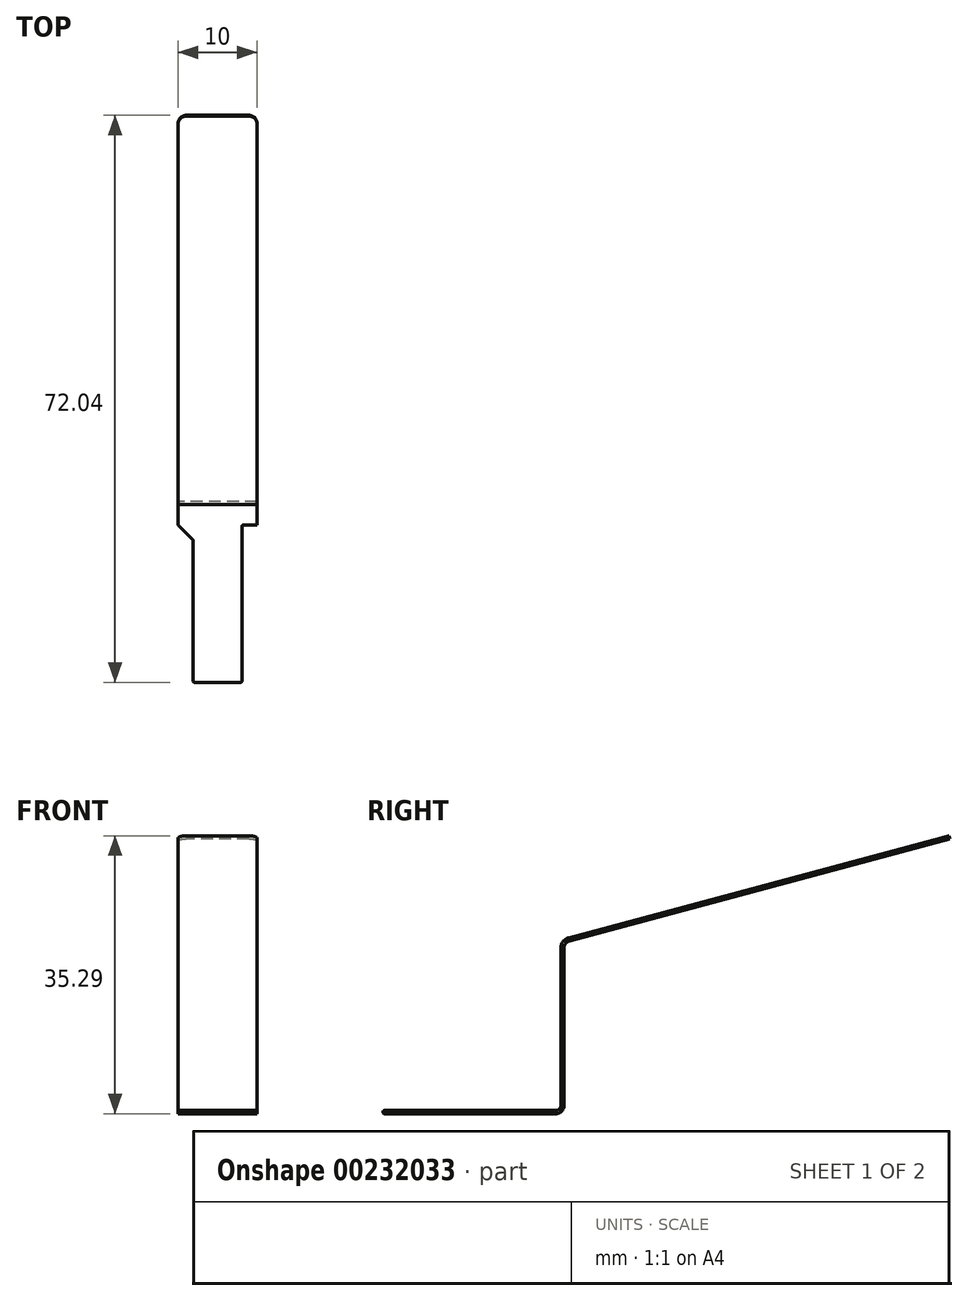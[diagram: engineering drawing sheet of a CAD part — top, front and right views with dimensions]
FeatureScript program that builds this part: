
annotation { "Feature Type Name" : "Feature", "Feature Type Description" : "" }
export const myFeature = defineFeature(function(context is Context, id is Id, definition is map)
    precondition{}
    {
        {
            var Q0;
            Q0=qCreatedBy(makeId("Front.planeOp"),FACE);
            var sketch = newSketch(context, id + "F0", { "sketchPlane" : qUnion([Q0])});
            skLineSegment(sketch, "E0.bottom", {"start": v(-3.12, 0) * mm, "end": v(3.12, 0) * mm});
            skLineSegment(sketch, "E0.top", {"start": v(-3.12, 0.4) * mm, "end": v(3.12, 0.4) * mm});
            skLineSegment(sketch, "E0.left", {"start": v(-3.12, 0) * mm, "end": v(-3.12, 0.4) * mm});
            skLineSegment(sketch, "E0.right", {"start": v(3.12, 0) * mm, "end": v(3.12, 0.4) * mm});
            skSolve(sketch);
        }
        {
            var Q0;
            Q0=qCreatedBy(makeId("Right.planeOp"),FACE);
            var sketch = newSketch(context, id + "F1", { "sketchPlane" : qUnion([Q0])});
            skLineSegment(sketch, "E1", {"start": v(0, 0) * mm, "end": v(20, 0) * mm});
            skSolve(sketch);
        }
        {
            var Q0;
            Q0=makeQuery(id+"F0.imprint","IMPRINT",FACE,{"disambiguationData":[TD([[makeQuery(id+"F0.imprint","IMPRINT",EDGE,{"derivedFrom":sQuery(id+"F0.wireOp",EDGE,"E0.bottom")}),1.0]])]});
            var Q1;
            Q1=sQuery(id+"F1.wireOp",EDGE,"E1");
            sweep(context, id + "F2", {"profiles" : qUnion([Q0]), "path" : qUnion([Q1])});
        }
        {
            var Q0;
            Q0=makeQuery(id+"F2.opSweep","CAP_FACE",FACE,{"disambiguationData":[OSD([sQuery(id+"F0.wireOp",EDGE,"E0.bottom"),sQuery(id+"F0.wireOp",EDGE,"E0.top"),sQuery(id+"F0.wireOp",EDGE,"E0.left"),sQuery(id+"F0.wireOp",EDGE,"E0.right"),sQuery(id+"F1.wireOp",VERTEX,"E1.end")])],"isStart":false});
            var sketch = newSketch(context, id + "F3", { "sketchPlane" : qUnion([Q0])});
            skLineSegment(sketch, "E2.bottom", {"start": v(-5, 0) * mm, "end": v(5, 0) * mm});
            skLineSegment(sketch, "E2.top", {"start": v(-5, 0.4) * mm, "end": v(5, 0.4) * mm});
            skLineSegment(sketch, "E2.left", {"start": v(-5, 0) * mm, "end": v(-5, 0.4) * mm});
            skLineSegment(sketch, "E2.right", {"start": v(5, 0) * mm, "end": v(5, 0.4) * mm});
            skSolve(sketch);
        }
        {
            var Q0;
            Q0=qCreatedBy(makeId("Right.planeOp"),FACE);
            var sketch = newSketch(context, id + "F4", { "sketchPlane" : qUnion([Q0])});
            skLineSegment(sketch, "E3", {"start": v(20, 0) * mm, "end": v(22, 0) * mm});
            skArc(sketch, "E4", {"start": v(22, 0) * mm, "mid": v(22.7, 0.3) * mm, "end": v(23, 1) * mm});
            skLineSegment(sketch, "E5", {"start": v(23, 1) * mm, "end": v(23, 21) * mm});
            skArc(sketch, "E6", {"start": v(23, 21) * mm, "mid": v(23.2, 21.6) * mm, "end": v(23.74, 21.97) * mm});
            skLineSegment(sketch, "E7", {"start": v(23.74, 21.97) * mm, "end": v(72.04, 34.9) * mm});
            skSolve(sketch);
        }
        {
            var Q0;
            {var subQ2=sQuery(id+"F3.wireOp",EDGE,"E2.left");Q0=makeQuery(id+"F3.imprint","IMPRINT",FACE,{"disambiguationData":[TD([[makeQuery(id+"F3.imprint","IMPRINT",EDGE,{"derivedFrom":subQ2}),-1.0]])]});}
            var Q1;
            {var subQ1=sQuery(id+"F1.wireOp",VERTEX,"E1.end");var subQ2=makeQuery(id+"F2.opSweep","CAP_EDGE",EDGE,{"disambiguationData":[OSD([sQuery(id+"F0.wireOp",EDGE,"E0.left"),subQ1])],"isStart":false});Q1=makeQuery(id+"F3.imprint","IMPRINT",FACE,{"disambiguationData":[TD([[makeQuery(id+"F3.imprint","IMPRINT",EDGE,{"derivedFrom":subQ2}),1.0]])]});}
            var Q2;
            {var subQ2=sQuery(id+"F3.wireOp",EDGE,"E2.right");Q2=makeQuery(id+"F3.imprint","IMPRINT",FACE,{"disambiguationData":[TD([[makeQuery(id+"F3.imprint","IMPRINT",EDGE,{"derivedFrom":subQ2}),1.0]])]});}
            var Q3;
            Q3=sQuery(id+"F4.wireOp",EDGE,"E3");
            var Q4;
            Q4=sQuery(id+"F4.wireOp",EDGE,"E4");
            var Q5;
            Q5=sQuery(id+"F4.wireOp",EDGE,"E5");
            var Q6;
            Q6=sQuery(id+"F4.wireOp",EDGE,"E7");
            var Q7;
            Q7=sQuery(id+"F4.wireOp",EDGE,"E6");
            sweep(context, id + "F5", {"operationType" : NewBodyOperationType.ADD, "profiles" : qUnion([Q0, Q1, Q2]), "path" : qUnion([Q3, Q4, Q5, Q6, Q7])});
        }
        {
            var Q0;
            Q0=makeQuery(id+"F2.opSweep","CAP_EDGE",EDGE,{"disambiguationData":[OSD([sQuery(id+"F0.wireOp",EDGE,"E0.right"),sQuery(id+"F1.wireOp",VERTEX,"E1.end")])],"isStart":false});
            var Q1;
            Q1=makeQuery(id+"F2.opSweep","CAP_EDGE",EDGE,{"disambiguationData":[OSD([sQuery(id+"F0.wireOp",EDGE,"E0.left"),sQuery(id+"F1.wireOp",VERTEX,"E1.end")])],"isStart":false});
            chamfer(context, id + "F6", {"entities" : qUnion([Q0, Q1]), "width" : 1.89 * mm, "tangentPropagation" : true});
        }
        {
            var Q0;
            Q0=makeQuery(id+"F2.opSweep","CAP_EDGE",EDGE,{"disambiguationData":[OSD([sQuery(id+"F0.wireOp",EDGE,"E0.right"),sQuery(id+"F1.wireOp",VERTEX,"E1.start")])],"isStart":true});
            var Q1;
            Q1=makeQuery(id+"F2.opSweep","CAP_EDGE",EDGE,{"disambiguationData":[OSD([sQuery(id+"F0.wireOp",EDGE,"E0.left"),sQuery(id+"F1.wireOp",VERTEX,"E1.start")])],"isStart":true});
            fillet(context, id + "F7", {"entities" : qUnion([Q0, Q1]), "radius" : 0.2 * mm, "tangentPropagation" : true, "allowEdgeOverflow" : false});
        }
        {
            var Q0;
            Q0=makeQuery(id+"F5.opSweep","CAP_EDGE",EDGE,{"disambiguationData":[OSD([sQuery(id+"F3.wireOp",EDGE,"E2.left"),sQuery(id+"F4.wireOp",VERTEX,"E7.end")])],"isStart":false});
            var Q1;
            Q1=makeQuery(id+"F5.opSweep","CAP_EDGE",EDGE,{"disambiguationData":[OSD([sQuery(id+"F3.wireOp",EDGE,"E2.right"),sQuery(id+"F4.wireOp",VERTEX,"E7.end")])],"isStart":false});
            fillet(context, id + "F8", {"entities" : qUnion([Q0, Q1]), "radius" : 1 * mm, "tangentPropagation" : true, "allowEdgeOverflow" : false});
        }
        {
            var Q0;
            Q0=makeQuery(id+"F2.opSweep","SWEPT_FACE",FACE,{"disambiguationData":[OSD([sQuery(id+"F0.wireOp",EDGE,"E0.right"),sQuery(id+"F1.wireOp",EDGE,"E1")])]});
            var Q1;
            Q1=makeQuery(id+"F6.opChamfer","BLEND_FACE",FACE,{"disambiguationData":[OSD([sQuery(id+"F0.wireOp",EDGE,"E0.left"),sQuery(id+"F1.wireOp",VERTEX,"E1.end")])]});
            fillet(context, id + "F9", {"entities" : qUnion([Q0, Q1]), "radius" : 0.2 * mm, "tangentPropagation" : true, "allowEdgeOverflow" : false});
        }
    });
